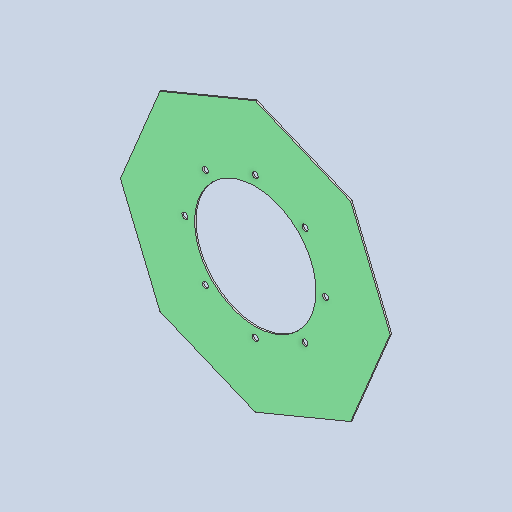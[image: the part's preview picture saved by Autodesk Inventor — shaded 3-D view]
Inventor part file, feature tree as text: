
AUTODESK INVENTOR PART (.ipt)
format: ipt  version: 2025 (Build 290162010, 162A)  size: 170,496 bytes
history: native  units: mm
features: sketch x2, other x2, sheet_metal_op x1, extrude x1, pattern_circular x1
ambient origin geometry x8: Origin, YZ Plane, XZ Plane, XY Plane, X Axis, Y Axis, Z Axis, Center Point
bodies: Solid1 (feature_tree)
feature tree (7):
  sheet_metal_op  "Face1"
  extrude  "Extrusion1"  Depth=3.0mm
  pattern_circular  "Circular Pattern1"  [2 undecoded]
  sketch  "Sketch2"  dims[d15=3.0mm d16=12.5mm]
  other  "Plate1"
  sketch  "Sketch4"  dims[d17=145.0mm d18=10.0mm d19=0.0mm d20=80.0mm d21=360.0deg d23=513.0mm d26=250.0mm]
  other  "Definition1"
note: 2 required parameter values undecoded (feature->parameter linkage not recoverable at this tier; creation-order binding heuristic only, values carry confidence <= 0.55)
